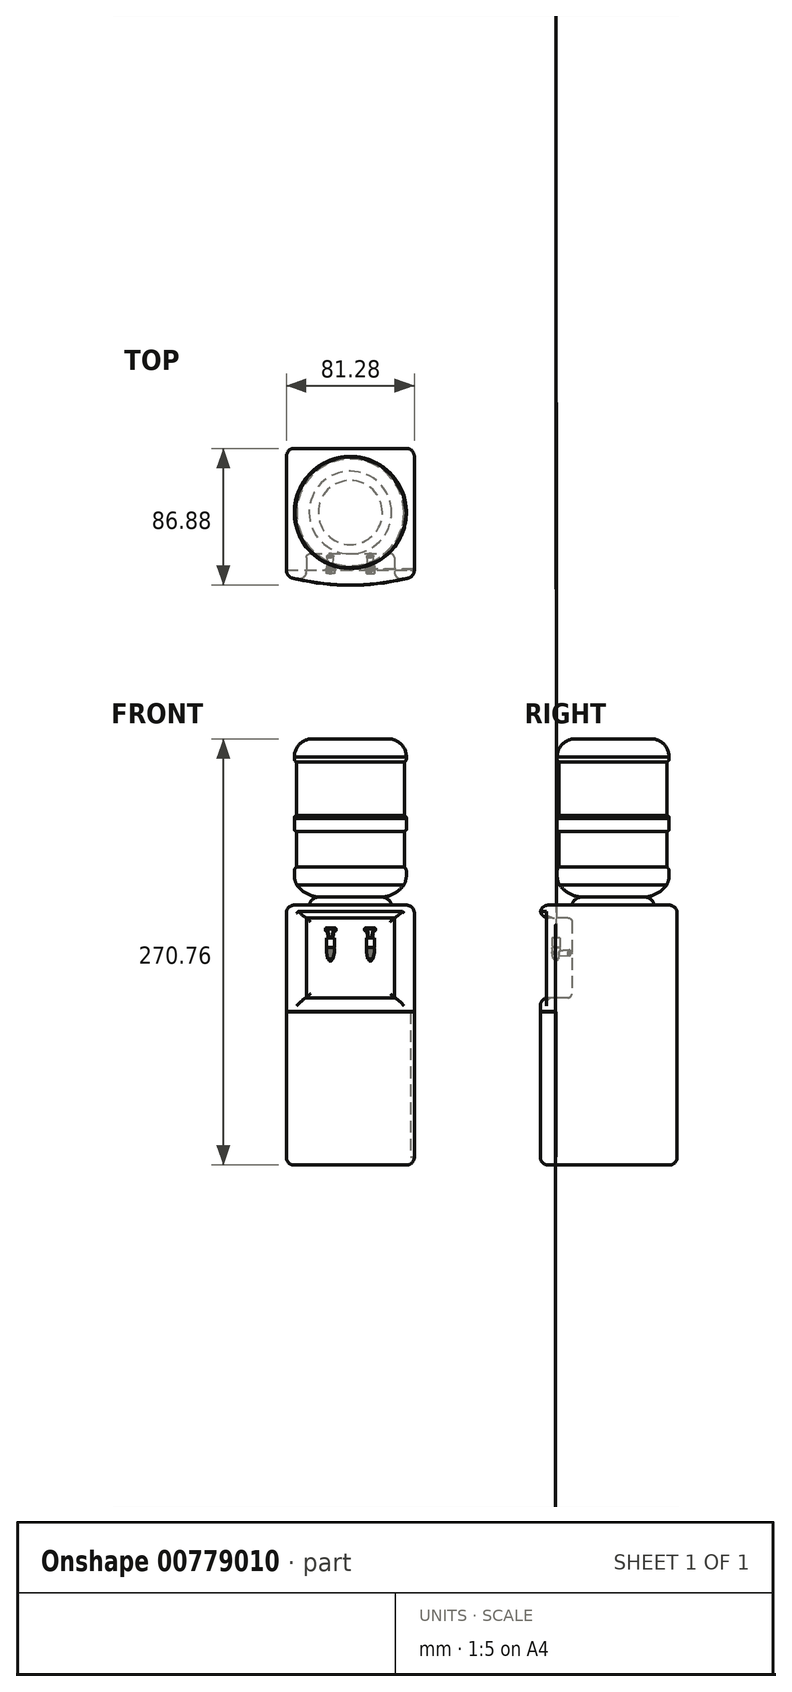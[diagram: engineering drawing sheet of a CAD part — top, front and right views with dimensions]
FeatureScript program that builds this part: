
annotation { "Feature Type Name" : "Feature", "Feature Type Description" : "" }
export const myFeature = defineFeature(function(context is Context, id is Id, definition is map)
    precondition{}
    {
        {
            var Q0;
            Q0=qCreatedBy(makeId("Front.planeOp"),FACE);
            var sketch = newSketch(context, id + "F0", { "sketchPlane" : qUnion([Q0])});
            skLineSegment(sketch, "E0", {"start": v(0, 95.92) * mm, "end": v(24.1, 95.92) * mm});
            skLineSegment(sketch, "E1", {"start": v(0, 11.85) * mm, "end": v(35.56, 11.85) * mm, "construction": true});
            skLineSegment(sketch, "E2", {"start": v(0, 83.22) * mm, "end": v(35.56, 83.22) * mm, "construction": true});
            skLineSegment(sketch, "E3", {"start": v(0, 81.19) * mm, "end": v(34.29, 81.11) * mm, "construction": true});
            skPoint(sketch, "E4.visualSharp", {"position": v(35.56, 95.92) * mm});
            skArc(sketch, "E4.filletArc", {"start": v(35.53, 84.46) * mm, "mid": v(32.2, 92.56) * mm, "end": v(24.1, 95.92) * mm});
            skLineSegment(sketch, "E5", {"start": v(35.53, 84.46) * mm, "end": v(35.56, 83.22) * mm});
            skLineSegment(sketch, "E6", {"start": v(0, 47.4) * mm, "end": v(38.08, 47.32) * mm, "construction": true});
            skLineSegment(sketch, "E7", {"start": v(34.29, 81.11) * mm, "end": v(34.29, 47.33) * mm});
            skLineSegment(sketch, "E8", {"start": v(0, 45.37) * mm, "end": v(35.56, 45.37) * mm, "construction": true});
            skLineSegment(sketch, "E9", {"start": v(0, 38.52) * mm, "end": v(35.56, 38.44) * mm, "construction": true});
            skLineSegment(sketch, "E10", {"start": v(0, 37.25) * mm, "end": v(34.29, 37.17) * mm, "construction": true});
            skArc(sketch, "E11", {"start": v(35.56, 83.22) * mm, "mid": v(35.23, 81.98) * mm, "end": v(34.29, 81.11) * mm});
            skArc(sketch, "E12", {"start": v(35.56, 45.37) * mm, "mid": v(35.23, 46.55) * mm, "end": v(34.29, 47.33) * mm});
            skArc(sketch, "E13", {"start": v(34.29, 37.17) * mm, "mid": v(35.19, 37.54) * mm, "end": v(35.56, 38.44) * mm});
            skLineSegment(sketch, "E14", {"start": v(35.56, 45.37) * mm, "end": v(35.56, 38.44) * mm});
            skLineSegment(sketch, "E15", {"start": v(0, 14.39) * mm, "end": v(34.3, 14.39) * mm, "construction": true});
            skLineSegment(sketch, "E16", {"start": v(0, 2.96) * mm, "end": v(33.95, 2.96) * mm, "construction": true});
            skLineSegment(sketch, "E17", {"start": v(34.29, 37.17) * mm, "end": v(34.3, 14.39) * mm});
            skLineSegment(sketch, "E18", {"start": v(0, -4.66) * mm, "end": v(20.35, -4.66) * mm, "construction": true});
            skLineSegment(sketch, "E19", {"start": v(0, -9.74) * mm, "end": v(26.2, -9.74) * mm});
            skArc(sketch, "E20", {"start": v(35.56, 11.85) * mm, "mid": v(35.22, 13.27) * mm, "end": v(34.3, 14.39) * mm});
            skLineSegment(sketch, "E21", {"start": v(35.56, 11.85) * mm, "end": v(35.57, 9.23) * mm});
            skArc(sketch, "E22", {"start": v(33.95, 2.96) * mm, "mid": v(35.16, 5.99) * mm, "end": v(35.57, 9.23) * mm});
            skArc(sketch, "E23", {"start": v(20.35, -4.66) * mm, "mid": v(27.95, -2.29) * mm, "end": v(33.95, 2.96) * mm});
            skArc(sketch, "E24", {"start": v(26.2, -9.74) * mm, "mid": v(24.13, -6.22) * mm, "end": v(20.35, -4.66) * mm});
            skLineSegment(sketch, "E25", {"start": v(0, 95.92) * mm, "end": v(0, -9.74) * mm});
            skSolve(sketch);
        }
        {
            var Q0;
            Q0=qSketchRegion(id+"F0",true);
            var Q1;
            Q1=sQuery(id+"F0.wireOp",EDGE,"E25");
            revolve(context, id + "F1", {"surfaceOperationType" : NewSurfaceOperationType.NEW, "entities" : qUnion([Q0]), "axis" : qUnion([Q1]), "revolveType" : RevolveType.FULL});
        }
        {
            var Q0;
            Q0=makeQuery(id+"F1.opRevolve","SWEPT_FACE",FACE,{"disambiguationData":[OSD([sQuery(id+"F0.wireOp",EDGE,"E19")])]});
            cPlane(context, id + "F2", {"entities" : qUnion([Q0]), "cplaneType" : CPlaneType.OFFSET, "offset" : 0 * mm, "width" : 152.4 * mm, "height" : 152.4 * mm});
        }
        {
            var Q0;
            Q0=qCreatedBy(id+"F2.planeOp",FACE);
            var sketch = newSketch(context, id + "F3", { "sketchPlane" : qUnion([Q0])});
            skLineSegment(sketch, "E26.top", {"start": v(-40.64, -40.64) * mm, "end": v(40.64, -40.64) * mm});
            skLineSegment(sketch, "E26.left", {"start": v(-40.64, 40.64) * mm, "end": v(-40.64, -40.64) * mm});
            skLineSegment(sketch, "E26.right", {"start": v(40.64, 40.64) * mm, "end": v(40.64, -40.64) * mm});
            skArc(sketch, "E27", {"start": v(40.64, 40.64) * mm, "mid": v(0, 46.24) * mm, "end": v(-40.64, 40.64) * mm});
            skSolve(sketch);
        }
        {
            var Q0;
            Q0=qSketchRegion(id+"F3",true);
            extrude(context, id + "F4", {"entities" : qUnion([Q0]), "operationType" : NewBodyOperationType.ADD, "depth" : 165.1 * mm, "offsetDistance" : 25.4 * mm});
        }
        {
            var Q0;
            Q0=qCreatedBy(makeId("Front.planeOp"),FACE);
            cPlane(context, id + "F5", {"entities" : qUnion([Q0]), "cplaneType" : CPlaneType.OFFSET, "offset" : 46.48 * mm, "width" : 152.4 * mm, "height" : 152.4 * mm});
        }
        {
            var Q0;
            Q0=qCreatedBy(id+"F5.planeOp",FACE);
            var sketch = newSketch(context, id + "F6", { "sketchPlane" : qUnion([Q0])});
            skLineSegment(sketch, "E28.bottom", {"start": v(-27.94, -17.78) * mm, "end": v(27.94, -17.78) * mm});
            skLineSegment(sketch, "E28.top", {"start": v(-27.94, -68.58) * mm, "end": v(27.94, -68.58) * mm});
            skLineSegment(sketch, "E28.left", {"start": v(-27.94, -17.78) * mm, "end": v(-27.94, -68.58) * mm});
            skLineSegment(sketch, "E28.right", {"start": v(27.94, -17.78) * mm, "end": v(27.94, -68.58) * mm});
            skSolve(sketch);
        }
        {
            var Q0;
            Q0=qSketchRegion(id+"F6",true);
            extrude(context, id + "F7", {"entities" : qUnion([Q0]), "operationType" : NewBodyOperationType.REMOVE, "oppositeDirection" : true, "depth" : 20.32 * mm, "offsetDistance" : 25.4 * mm});
        }
        {
            var Q0;
            Q0=makeQuery(id+"F4.opExtrude","CAP_EDGE",EDGE,{"disambiguationData":[OSD([sQuery(id+"F3.wireOp",EDGE,"E26.left")])],"isStart":true});
            var Q1;
            Q1=makeQuery(id+"F4.opExtrude","SWEPT_EDGE",EDGE,{"disambiguationData":[OSD([sQuery(id+"F3.wireOp",EDGE,"E26.top"),sQuery(id+"F3.wireOp",EDGE,"E26.left")])]});
            var Q2;
            Q2=makeQuery(id+"F4.opExtrude","SWEPT_EDGE",EDGE,{"disambiguationData":[OSD([sQuery(id+"F3.wireOp",EDGE,"E26.left"),sQuery(id+"F3.wireOp",EDGE,"E27")])]});
            var Q3;
            Q3=makeQuery(id+"F4.opExtrude","CAP_EDGE",EDGE,{"disambiguationData":[OSD([sQuery(id+"F3.wireOp",EDGE,"E27")])],"isStart":true});
            var Q4;
            Q4=makeQuery(id+"F4.opExtrude","SWEPT_EDGE",EDGE,{"disambiguationData":[OSD([sQuery(id+"F3.wireOp",EDGE,"E26.right"),sQuery(id+"F3.wireOp",EDGE,"E27")])]});
            var Q5;
            Q5=makeQuery(id+"F4.opExtrude","CAP_EDGE",EDGE,{"disambiguationData":[OSD([sQuery(id+"F3.wireOp",EDGE,"E26.right")])],"isStart":true});
            var Q6;
            Q6=makeQuery(id+"F4.opExtrude","SWEPT_EDGE",EDGE,{"disambiguationData":[OSD([sQuery(id+"F3.wireOp",EDGE,"E26.top"),sQuery(id+"F3.wireOp",EDGE,"E26.right")])]});
            var Q7;
            Q7=makeQuery(id+"F4.opExtrude","CAP_EDGE",EDGE,{"disambiguationData":[OSD([sQuery(id+"F3.wireOp",EDGE,"E26.right")])],"isStart":false});
            var Q8;
            Q8=makeQuery(id+"F4.opExtrude","CAP_EDGE",EDGE,{"disambiguationData":[OSD([sQuery(id+"F3.wireOp",EDGE,"E27")])],"isStart":false});
            var Q9;
            Q9=makeQuery(id+"F4.opExtrude","CAP_EDGE",EDGE,{"disambiguationData":[OSD([sQuery(id+"F3.wireOp",EDGE,"E26.left")])],"isStart":false});
            var Q10;
            Q10=makeQuery(id+"F4.opExtrude","CAP_EDGE",EDGE,{"disambiguationData":[OSD([sQuery(id+"F3.wireOp",EDGE,"E26.top")])],"isStart":true});
            var Q11;
            Q11=makeQuery(id+"F4.opExtrude","CAP_EDGE",EDGE,{"disambiguationData":[OSD([sQuery(id+"F3.wireOp",EDGE,"E26.top")])],"isStart":false});
            fillet(context, id + "F8", {"entities" : qUnion([Q0, Q1, Q2, Q3, Q4, Q5, Q6, Q7, Q8, Q9, Q10, Q11]), "radius" : 5.08 * mm, "tangentPropagation" : true, "allowEdgeOverflow" : false});
        }
        {
            var Q0;
            Q0=qCreatedBy(id+"F5.planeOp",FACE);
            var sketch = newSketch(context, id + "F9", { "sketchPlane" : qUnion([Q0])});
            skLineSegment(sketch, "E29.bottom", {"start": v(-49.64, -77.18) * mm, "end": v(53.25, -77.18) * mm});
            skLineSegment(sketch, "E29.top", {"start": v(-49.64, -77.69) * mm, "end": v(53.25, -77.69) * mm});
            skLineSegment(sketch, "E29.left", {"start": v(-49.64, -77.18) * mm, "end": v(-49.64, -77.69) * mm});
            skLineSegment(sketch, "E29.right", {"start": v(53.25, -77.18) * mm, "end": v(53.25, -77.69) * mm});
            skSolve(sketch);
        }
        {
            var Q0;
            Q0=qSketchRegion(id+"F9",true);
            extrude(context, id + "F10", {"entities" : qUnion([Q0]), "operationType" : NewBodyOperationType.REMOVE, "oppositeDirection" : true, "depth" : 9.9 * mm, "offsetDistance" : 25.4 * mm});
        }
        {
            var Q0;
            Q0=makeQuery(id+"F7.boolean.opBoolean","COPY",FACE,{"derivedFrom":makeQuery(id+"F7.opExtrude","CAP_FACE",FACE,{"disambiguationData":[OSD([sQuery(id+"F6.wireOp",EDGE,"E28.bottom"),sQuery(id+"F6.wireOp",EDGE,"E28.top"),sQuery(id+"F6.wireOp",EDGE,"E28.left"),sQuery(id+"F6.wireOp",EDGE,"E28.right")])],"isStart":false})});
            fillet(context, id + "F11", {"entities" : qUnion([Q0]), "radius" : 2.54 * mm, "tangentPropagation" : true, "allowEdgeOverflow" : false});
        }
        {
            var Q0;
            Q0=makeQuery(id+"F7.boolean.opBoolean","INTERSECT",EDGE,{"derivedFrom":[makeQuery(id+"F4.opExtrude","SWEPT_FACE",FACE,{"disambiguationData":[OSD([sQuery(id+"F3.wireOp",EDGE,"E27")])]}),makeQuery(id+"F7.opExtrude","SWEPT_FACE",FACE,{"disambiguationData":[OSD([sQuery(id+"F6.wireOp",EDGE,"E28.bottom")])]})]});
            var Q1;
            Q1=makeQuery(id+"F7.boolean.opBoolean","INTERSECT",EDGE,{"derivedFrom":[makeQuery(id+"F4.opExtrude","SWEPT_FACE",FACE,{"disambiguationData":[OSD([sQuery(id+"F3.wireOp",EDGE,"E27")])]}),makeQuery(id+"F7.opExtrude","SWEPT_FACE",FACE,{"disambiguationData":[OSD([sQuery(id+"F6.wireOp",EDGE,"E28.right")])]})]});
            var Q2;
            Q2=makeQuery(id+"F7.boolean.opBoolean","INTERSECT",EDGE,{"derivedFrom":[makeQuery(id+"F4.opExtrude","SWEPT_FACE",FACE,{"disambiguationData":[OSD([sQuery(id+"F3.wireOp",EDGE,"E27")])]}),makeQuery(id+"F7.opExtrude","SWEPT_FACE",FACE,{"disambiguationData":[OSD([sQuery(id+"F6.wireOp",EDGE,"E28.top")])]})]});
            var Q3;
            Q3=makeQuery(id+"F7.boolean.opBoolean","INTERSECT",EDGE,{"derivedFrom":[makeQuery(id+"F4.opExtrude","SWEPT_FACE",FACE,{"disambiguationData":[OSD([sQuery(id+"F3.wireOp",EDGE,"E27")])]}),makeQuery(id+"F7.opExtrude","SWEPT_FACE",FACE,{"disambiguationData":[OSD([sQuery(id+"F6.wireOp",EDGE,"E28.left")])]})]});
            fillet(context, id + "F12", {"entities" : qUnion([Q0, Q1, Q2, Q3]), "radius" : 5.08 * mm, "tangentPropagation" : true, "allowEdgeOverflow" : false});
        }
        {
            var Q0;
            Q0=makeQuery(id+"F4.opExtrude","SWEPT_FACE",FACE,{"disambiguationData":[OSD([sQuery(id+"F3.wireOp",EDGE,"E26.right")])]});
            var sketch = newSketch(context, id + "F13", { "sketchPlane" : qUnion([Q0])});
            skLineSegment(sketch, "E30.bottom", {"start": v(-36.23, -77.69) * mm, "end": v(-36.74, -77.69) * mm});
            skLineSegment(sketch, "E30.top", {"start": v(-36.23, -169.76) * mm, "end": v(-36.74, -169.76) * mm});
            skLineSegment(sketch, "E30.left", {"start": v(-36.23, -77.69) * mm, "end": v(-36.23, -169.76) * mm});
            skLineSegment(sketch, "E30.right", {"start": v(-36.74, -77.69) * mm, "end": v(-36.74, -169.76) * mm});
            skSolve(sketch);
        }
        {
            var Q0;
            Q0=makeQuery(id+"F13.imprint","IMPRINT",FACE,{"disambiguationData":[TD([[makeQuery(id+"F13.imprint","IMPRINT",EDGE,{"derivedFrom":sQuery(id+"F13.wireOp",EDGE,"E30.bottom")}),-1.0]])]});
            extrude(context, id + "F14", {"entities" : qUnion([Q0]), "operationType" : NewBodyOperationType.REMOVE, "oppositeDirection" : true, "depth" : 2.6 * mm, "offsetDistance" : 25.4 * mm});
        }
        {
            var Q0;
            Q0=qCreatedBy(makeId("Top.planeOp"),FACE);
            cPlane(context, id + "F15", {"entities" : qUnion([Q0]), "cplaneType" : CPlaneType.OFFSET, "offset" : 40.13 * mm, "oppositeDirection" : true, "width" : 152.4 * mm, "height" : 152.4 * mm});
        }
        {
            var Q0;
            Q0=qCreatedBy(id+"F15.planeOp",FACE);
            var sketch = newSketch(context, id + "F16", { "sketchPlane" : qUnion([Q0])});
            skLineSegment(sketch, "E31", {"start": v(-14.73, -26.16) * mm, "end": v(-14.22, -36.32) * mm});
            skLineSegment(sketch, "E32", {"start": v(-12.7, -26.16) * mm, "end": v(-12.7, -36.32) * mm});
            skLineSegment(sketch, "E33", {"start": v(-14.73, -26.16) * mm, "end": v(-12.7, -26.16) * mm});
            skLineSegment(sketch, "E34", {"start": v(-14.22, -36.32) * mm, "end": v(-12.7, -36.32) * mm});
            skSolve(sketch);
        }
        {
            var Q0;
            Q0=makeQuery(id+"F16.imprint","IMPRINT",FACE,{"disambiguationData":[TD([[makeQuery(id+"F16.imprint","IMPRINT",EDGE,{"derivedFrom":sQuery(id+"F16.wireOp",EDGE,"E31")}),1.0]])]});
            var Q1;
            Q1=sQuery(id+"F16.wireOp",EDGE,"E32");
            revolve(context, id + "F17", {"surfaceOperationType" : NewSurfaceOperationType.NEW, "entities" : qUnion([Q0]), "axis" : qUnion([Q1]), "revolveType" : RevolveType.FULL});
        }
        {
            var Q0;
            Q0=makeQuery(id+"F17.opRevolve","SWEPT_EDGE",EDGE,{"disambiguationData":[OSD([sQuery(id+"F16.wireOp",EDGE,"E31"),sQuery(id+"F16.wireOp",EDGE,"E33")])]});
            fillet(context, id + "F18", {"entities" : qUnion([Q0]), "radius" : 1.27 * mm, "tangentPropagation" : true, "allowEdgeOverflow" : false});
        }
        {
            var Q0;
            Q0=makeQuery(id+"F17.opRevolve","SWEPT_FACE",FACE,{"disambiguationData":[OSD([sQuery(id+"F16.wireOp",EDGE,"E34")])]});
            var sketch = newSketch(context, id + "F19", { "sketchPlane" : qUnion([Q0])});
            skLineSegment(sketch, "E35", {"start": v(-12.7, -40.13) * mm, "end": v(-12.7, -36.63) * mm});
            skLineSegment(sketch, "E36", {"start": v(-12.7, -36.63) * mm, "end": v(-10.72, -36.63) * mm});
            skLineSegment(sketch, "E37", {"start": v(-12.7, -40.13) * mm, "end": v(-12.7, -44) * mm});
            skLineSegment(sketch, "E38", {"start": v(-10.21, -37.11) * mm, "end": v(-10.1, -39.28) * mm});
            skLineSegment(sketch, "E39", {"start": v(-10.13, -39.53) * mm, "end": v(-10.94, -43.58) * mm});
            skLineSegment(sketch, "E40", {"start": v(-12.7, -44) * mm, "end": v(-12.7, -45.1) * mm});
            skLineSegment(sketch, "E41", {"start": v(-12.7, -45.1) * mm, "end": v(-12.1, -45.1) * mm});
            skLineSegment(sketch, "E42", {"start": v(-11.85, -44.85) * mm, "end": v(-11.85, -44.05) * mm});
            skLineSegment(sketch, "E43", {"start": v(-11.8, -44) * mm, "end": v(-11.44, -44) * mm});
            skPoint(sketch, "E44.visualSharp", {"position": v(-10.24, -36.63) * mm});
            skArc(sketch, "E44.filletArc", {"start": v(-10.21, -37.11) * mm, "mid": v(-10.37, -36.77) * mm, "end": v(-10.72, -36.63) * mm});
            skPoint(sketch, "E45.visualSharp", {"position": v(-10.1, -39.4) * mm});
            skArc(sketch, "E45.filletArc", {"start": v(-10.13, -39.53) * mm, "mid": v(-10.11, -39.4) * mm, "end": v(-10.1, -39.28) * mm});
            skPoint(sketch, "E46.visualSharp", {"position": v(-11.02, -44) * mm});
            skArc(sketch, "E46.filletArc", {"start": v(-11.44, -44) * mm, "mid": v(-11.12, -43.88) * mm, "end": v(-10.94, -43.58) * mm});
            skPoint(sketch, "E47.visualSharp", {"position": v(-11.85, -44) * mm});
            skArc(sketch, "E47.filletArc", {"start": v(-11.8, -44) * mm, "mid": v(-11.83, -44) * mm, "end": v(-11.85, -44.05) * mm});
            skPoint(sketch, "E48.visualSharp", {"position": v(-11.85, -45.1) * mm});
            skArc(sketch, "E48.filletArc", {"start": v(-12.1, -45.1) * mm, "mid": v(-11.92, -45.03) * mm, "end": v(-11.85, -44.85) * mm});
            skSolve(sketch);
        }
        {
            var Q0;
            {var subQ4=sQuery(id+"F19.wireOp",EDGE,"E36");Q0=makeQuery(id+"F19.imprint","IMPRINT",FACE,{"disambiguationData":[TD([[makeQuery(id+"F19.imprint","IMPRINT",EDGE,{"derivedFrom":subQ4}),-1.0]])]});}
            var Q1;
            Q1=sQuery(id+"F19.wireOp",EDGE,"E35");
            revolve(context, id + "F20", {"operationType" : NewBodyOperationType.ADD, "surfaceOperationType" : NewSurfaceOperationType.NEW, "entities" : qUnion([Q0]), "axis" : qUnion([Q1]), "revolveType" : RevolveType.FULL});
        }
        {
            var Q0;
            Q0=qCreatedBy(makeId("Right.planeOp"),FACE);
            cPlane(context, id + "F21", {"entities" : qUnion([Q0]), "cplaneType" : CPlaneType.OFFSET, "offset" : 12.7 * mm, "oppositeDirection" : true, "width" : 152.4 * mm, "height" : 152.4 * mm});
        }
        {
            var Q0;
            Q0=makeQuery(id+"F7.boolean.opBoolean","COPY",FACE,{"derivedFrom":makeQuery(id+"F7.opExtrude","CAP_FACE",FACE,{"disambiguationData":[OSD([sQuery(id+"F6.wireOp",EDGE,"E28.bottom"),sQuery(id+"F6.wireOp",EDGE,"E28.top"),sQuery(id+"F6.wireOp",EDGE,"E28.left"),sQuery(id+"F6.wireOp",EDGE,"E28.right")])],"isStart":false})});
            cPlane(context, id + "F22", {"entities" : qUnion([Q0]), "cplaneType" : CPlaneType.OFFSET, "offset" : 10.16 * mm, "width" : 152.4 * mm, "height" : 152.4 * mm});
        }
        {
            var Q0;
            Q0=qCreatedBy(id+"F21.planeOp",FACE);
            var sketch = newSketch(context, id + "F23", { "sketchPlane" : qUnion([Q0])});
            skLineSegment(sketch, "E49.bottom", {"start": v(-33.78, -30.63) * mm, "end": v(-38.86, -30.63) * mm});
            skLineSegment(sketch, "E49.top", {"start": v(-33.78, -36.63) * mm, "end": v(-36.83, -36.63) * mm});
            skLineSegment(sketch, "E49.left", {"start": v(-33.78, -30.63) * mm, "end": v(-33.78, -36.63) * mm});
            skLineSegment(sketch, "E49.right", {"start": v(-38.86, -30.63) * mm, "end": v(-38.86, -34.6) * mm});
            skPoint(sketch, "E50.visualSharp", {"position": v(-38.86, -36.63) * mm});
            skArc(sketch, "E50.filletArc", {"start": v(-38.86, -34.6) * mm, "mid": v(-38.27, -36.04) * mm, "end": v(-36.83, -36.63) * mm});
            skSolve(sketch);
        }
        {
            var Q0;
            Q0=makeQuery(id+"F23.imprint","IMPRINT",FACE,{"disambiguationData":[TD([[makeQuery(id+"F23.imprint","IMPRINT",EDGE,{"derivedFrom":sQuery(id+"F23.wireOp",EDGE,"E49.bottom")}),1.0]])]});
            extrude(context, id + "F24", {"entities" : qUnion([Q0]), "operationType" : NewBodyOperationType.ADD, "depth" : 2.54 * mm, "offsetDistance" : 25.4 * mm, "hasSecondDirection" : true, "secondDirectionOppositeDirection" : true, "secondDirectionDepth" : 2.54 * mm});
        }
        {
            var Q0;
            Q0=qCreatedBy(id+"F22.planeOp",FACE);
            var sketch = newSketch(context, id + "F25", { "sketchPlane" : qUnion([Q0])});
            skLineSegment(sketch, "E51.bottom", {"start": v(-15.34, -24.56) * mm, "end": v(-9.6, -24.56) * mm});
            skLineSegment(sketch, "E51.left", {"start": v(-15.6, -24.8) * mm, "end": v(-15.6, -25.78) * mm});
            skLineSegment(sketch, "E51.right", {"start": v(-9.34, -24.8) * mm, "end": v(-9.34, -25.74) * mm});
            skLineSegment(sketch, "E52", {"start": v(-14.5, -26.24) * mm, "end": v(-13.66, -30.63) * mm});
            skLineSegment(sketch, "E53", {"start": v(-11.3, -30.63) * mm, "end": v(-10.78, -26.22) * mm});
            skLineSegment(sketch, "E54", {"start": v(-15.34, -26.03) * mm, "end": v(-14.75, -26.03) * mm});
            skLineSegment(sketch, "E55", {"start": v(-10.53, -26) * mm, "end": v(-9.6, -26) * mm});
            skPoint(sketch, "E56.visualSharp", {"position": v(-10.75, -26) * mm});
            skArc(sketch, "E56.filletArc", {"start": v(-10.53, -26) * mm, "mid": v(-10.7, -26.06) * mm, "end": v(-10.78, -26.22) * mm});
            skPoint(sketch, "E57.visualSharp", {"position": v(-14.54, -26.03) * mm});
            skArc(sketch, "E57.filletArc", {"start": v(-14.5, -26.24) * mm, "mid": v(-14.58, -26.1) * mm, "end": v(-14.75, -26.03) * mm});
            skPoint(sketch, "E58.visualSharp", {"position": v(-15.6, -26.03) * mm});
            skArc(sketch, "E58.filletArc", {"start": v(-15.6, -25.78) * mm, "mid": v(-15.52, -25.96) * mm, "end": v(-15.34, -26.03) * mm});
            skPoint(sketch, "E59.visualSharp", {"position": v(-15.6, -24.56) * mm});
            skArc(sketch, "E59.filletArc", {"start": v(-15.34, -24.56) * mm, "mid": v(-15.52, -24.63) * mm, "end": v(-15.6, -24.8) * mm});
            skPoint(sketch, "E60.visualSharp", {"position": v(-9.34, -26) * mm});
            skArc(sketch, "E60.filletArc", {"start": v(-9.6, -26) * mm, "mid": v(-9.42, -25.92) * mm, "end": v(-9.34, -25.74) * mm});
            skPoint(sketch, "E61.visualSharp", {"position": v(-9.34, -24.56) * mm});
            skArc(sketch, "E61.filletArc", {"start": v(-9.34, -24.8) * mm, "mid": v(-9.42, -24.63) * mm, "end": v(-9.6, -24.56) * mm});
            skSolve(sketch);
        }
        {
            var Q0;
            Q0=makeQuery(id+"F24.opExtrude","SWEPT_FACE",FACE,{"disambiguationData":[OSD([sQuery(id+"F23.wireOp",EDGE,"E49.bottom")])]});
            cPlane(context, id + "F26", {"entities" : qUnion([Q0]), "cplaneType" : CPlaneType.OFFSET, "offset" : 0 * mm, "width" : 152.4 * mm, "height" : 152.4 * mm});
        }
        {
            var Q0;
            Q0=qCreatedBy(id+"F26.planeOp",FACE);
            var sketch = newSketch(context, id + "F27", { "sketchPlane" : qUnion([Q0])});
            skCircle(sketch, "E62", {"center": v(-13.67, -36.31) * mm, "radius": 0.25 * mm});
            skSolve(sketch);
        }
        {
            var Q0;
            Q0=makeQuery(id+"F27.imprint","IMPRINT",FACE,{"disambiguationData":[TD([[makeQuery(id+"F27.imprint","IMPRINT",EDGE,{"derivedFrom":sQuery(id+"F27.wireOp",EDGE,"E62")}),1.0]])]});
            var Q1;
            Q1=qConstructionFilter(qBodyType(qCreatedBy(id+"F25",EDGE),BodyType.WIRE),ConstructionObject.NO);
            sweep(context, id + "F28", {"operationType" : NewBodyOperationType.ADD, "profiles" : qUnion([Q0]), "path" : qUnion([Q1])});
        }
        {
            var Q0;
            Q0=makeQuery(id+"F17.opRevolve","SWEPT_BODY",BODY,{"disambiguationData":[OSD([sQuery(id+"F16.wireOp",EDGE,"E31"),sQuery(id+"F16.wireOp",EDGE,"E32"),sQuery(id+"F16.wireOp",EDGE,"E33"),sQuery(id+"F16.wireOp",EDGE,"E34")])]});
            var Q1;
            Q1=qCreatedBy(makeId("Right.planeOp"),FACE);
            mirror(context, id + "F29", {"entities" : qUnion([Q0]), "mirrorPlane" : qUnion([Q1])});
        }
    });
